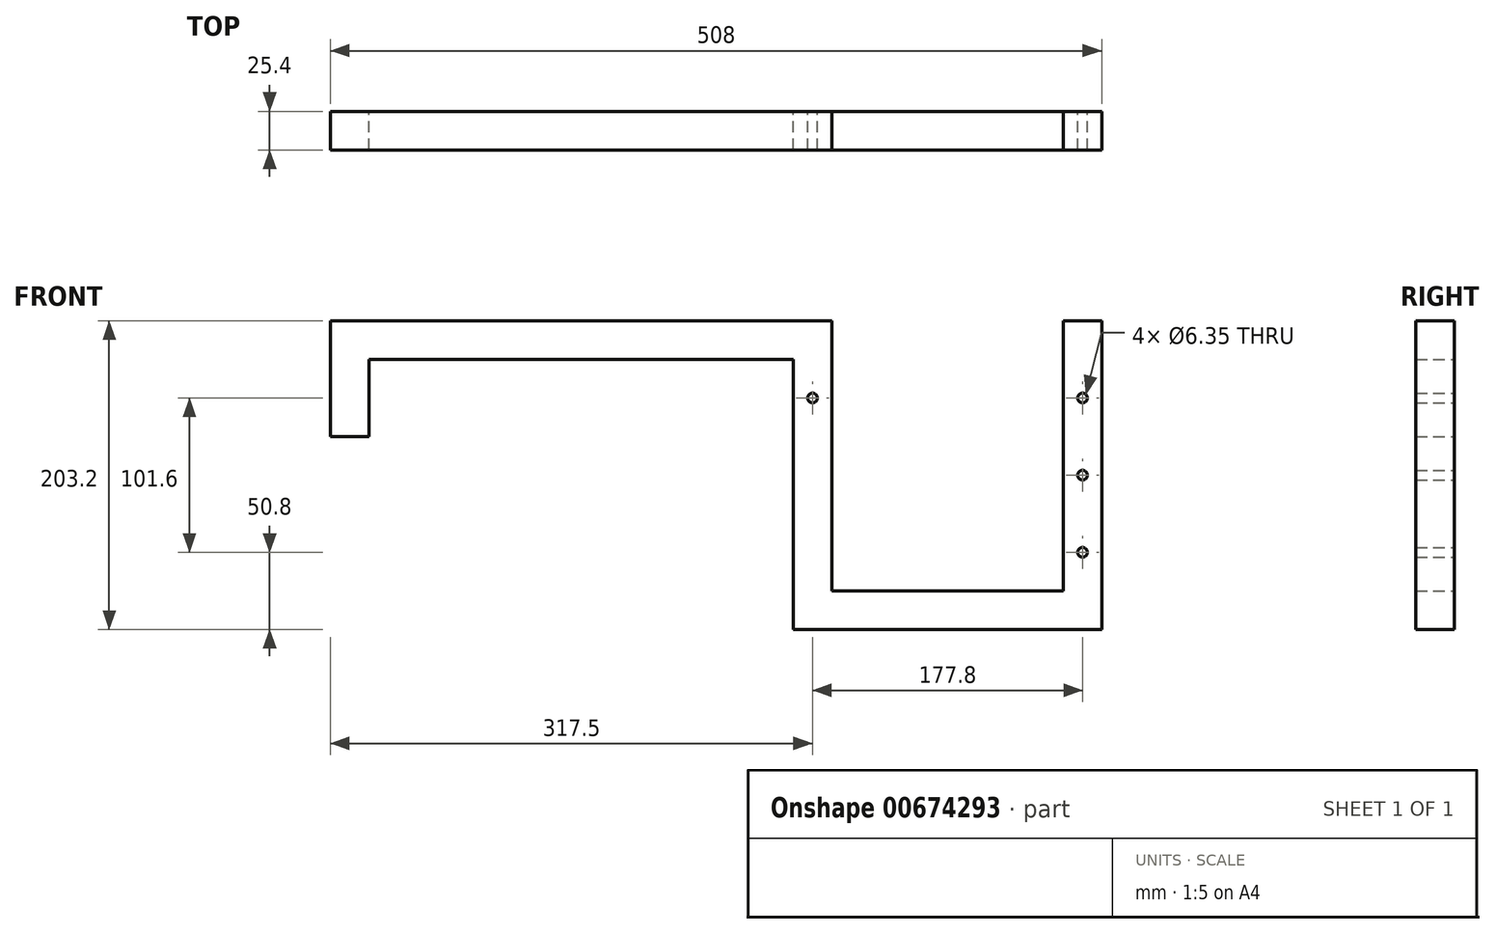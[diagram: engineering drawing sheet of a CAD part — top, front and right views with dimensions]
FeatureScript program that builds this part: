
annotation { "Feature Type Name" : "Feature", "Feature Type Description" : "" }
export const myFeature = defineFeature(function(context is Context, id is Id, definition is map)
    precondition{}
    {
        {
            var Q0;
            Q0=qCreatedBy(makeId("Front.planeOp"),FACE);
            var sketch = newSketch(context, id + "F0", { "sketchPlane" : qUnion([Q0])});
            skLineSegment(sketch, "E0.bottom", {"start": v(0, 0) * mm, "end": v(279.4, 0) * mm});
            skLineSegment(sketch, "E0.top", {"start": v(0, -25.4) * mm, "end": v(279.4, -25.4) * mm});
            skLineSegment(sketch, "E0.left", {"start": v(0, 0) * mm, "end": v(0, -25.4) * mm});
            skLineSegment(sketch, "E0.right", {"start": v(279.4, 0) * mm, "end": v(279.4, -25.4) * mm});
            skLineSegment(sketch, "E1.bottom", {"start": v(0, 0) * mm, "end": v(-25.4, 0) * mm});
            skLineSegment(sketch, "E1.top", {"start": v(0, -76.2) * mm, "end": v(-25.4, -76.2) * mm});
            skLineSegment(sketch, "E1.left", {"start": v(0, 0) * mm, "end": v(0, -76.2) * mm});
            skLineSegment(sketch, "E1.right", {"start": v(-25.4, 0) * mm, "end": v(-25.4, -76.2) * mm});
            skLineSegment(sketch, "E2.bottom", {"start": v(279.4, 0) * mm, "end": v(304.8, 0) * mm});
            skLineSegment(sketch, "E2.top", {"start": v(279.4, -203.2) * mm, "end": v(304.8, -203.2) * mm});
            skLineSegment(sketch, "E2.left", {"start": v(279.4, 0) * mm, "end": v(279.4, -203.2) * mm});
            skLineSegment(sketch, "E2.right", {"start": v(304.8, 0) * mm, "end": v(304.8, -203.2) * mm});
            skLineSegment(sketch, "E3.bottom", {"start": v(304.8, -203.2) * mm, "end": v(457.2, -203.2) * mm});
            skLineSegment(sketch, "E3.top", {"start": v(304.8, -177.8) * mm, "end": v(457.2, -177.8) * mm});
            skLineSegment(sketch, "E3.left", {"start": v(304.8, -203.2) * mm, "end": v(304.8, -177.8) * mm});
            skLineSegment(sketch, "E3.right", {"start": v(457.2, -203.2) * mm, "end": v(457.2, -177.8) * mm});
            skLineSegment(sketch, "E4.bottom", {"start": v(457.2, -203.2) * mm, "end": v(482.6, -203.2) * mm});
            skLineSegment(sketch, "E4.top", {"start": v(457.2, 0) * mm, "end": v(482.6, 0) * mm});
            skLineSegment(sketch, "E4.left", {"start": v(457.2, -203.2) * mm, "end": v(457.2, 0) * mm});
            skLineSegment(sketch, "E4.right", {"start": v(482.6, -203.2) * mm, "end": v(482.6, 0) * mm});
            skSolve(sketch);
        }
        {
            var Q0;
            Q0 = qSketchRegion(id + "F0", true);
            extrude(context, id + "F1", {"entities" : qUnion([Q0]), "endBound" : BoundingType.SYMMETRIC, "depth" : 25.4 * mm, "offsetDistance" : 25.4 * mm});
        }
        {
            var Q0;
            Q0=qCreatedBy(makeId("Front.planeOp"),FACE);
            var sketch = newSketch(context, id + "F2", { "sketchPlane" : qUnion([Q0])});
            skCircle(sketch, "E5", {"center": v(469.9, -101.6) * mm, "radius": 3.17 * mm});
            skCircle(sketch, "E6", {"center": v(469.9, -50.8) * mm, "radius": 3.18 * mm});
            skCircle(sketch, "E7", {"center": v(469.9, -152.4) * mm, "radius": 3.18 * mm});
            skCircle(sketch, "E8", {"center": v(292.1, -50.8) * mm, "radius": 3.18 * mm});
            skSolve(sketch);
        }
        {
            var Q0;
            Q0 = qSketchRegion(id + "F2", true);
            extrude(context, id + "F3", {"entities" : qUnion([Q0]), "operationType" : NewBodyOperationType.REMOVE, "endBound" : BoundingType.SYMMETRIC, "depth" : 25.4 * mm, "offsetDistance" : 25.4 * mm});
        }
    });
